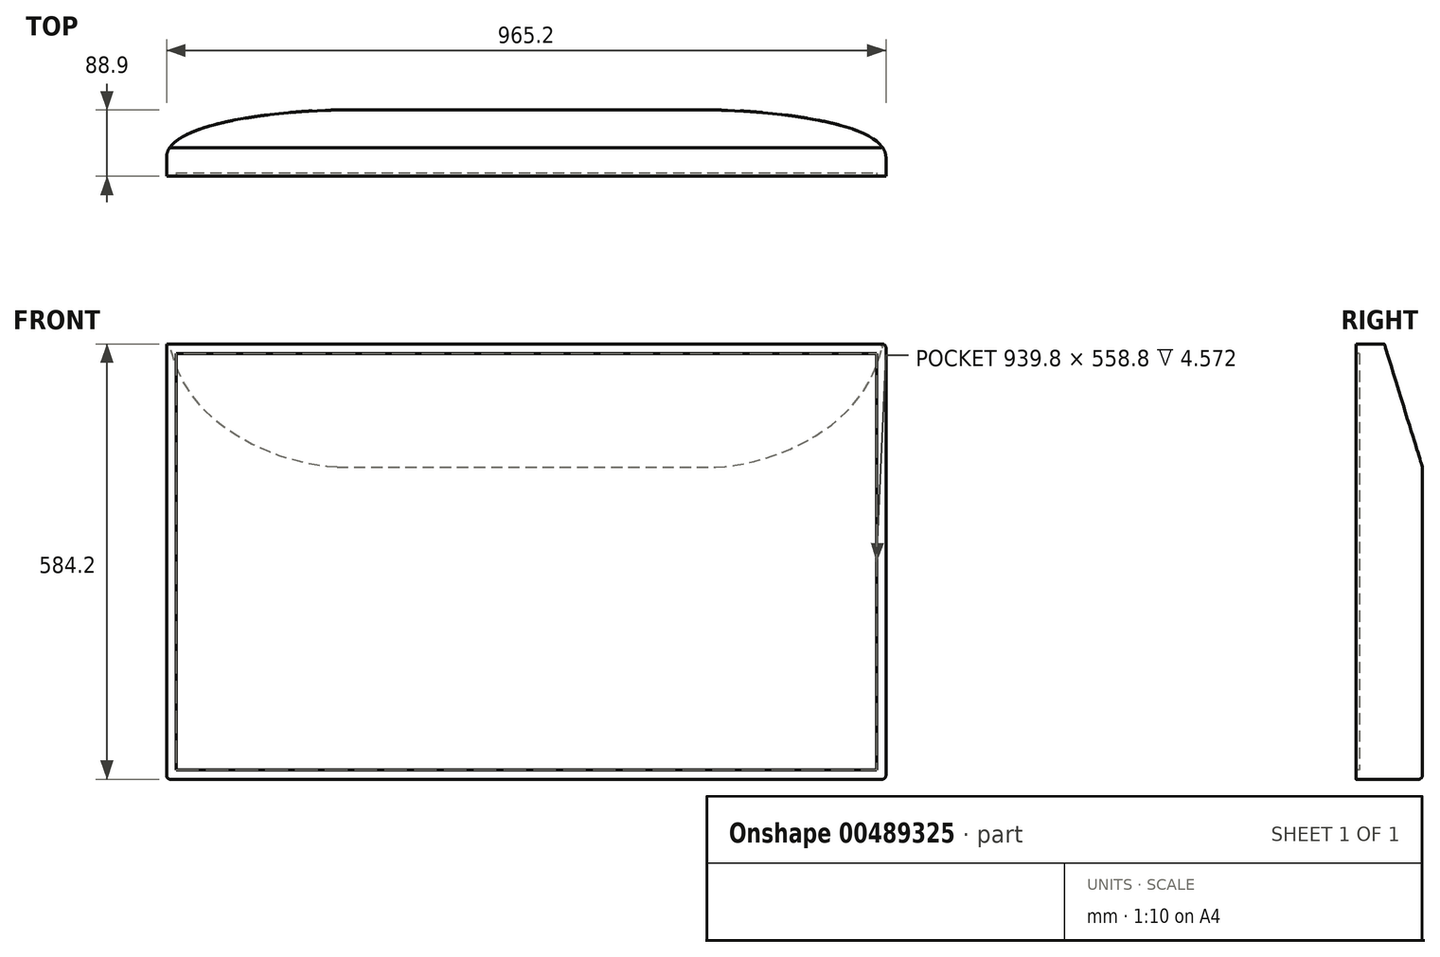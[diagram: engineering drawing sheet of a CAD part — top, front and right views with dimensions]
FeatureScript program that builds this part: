
annotation { "Feature Type Name" : "Feature", "Feature Type Description" : "" }
export const myFeature = defineFeature(function(context is Context, id is Id, definition is map)
    precondition{}
    {
        {
            var Q0;
            Q0=qCreatedBy(makeId("Top.planeOp"),FACE);
            var sketch = newSketch(context, id + "F0", { "sketchPlane" : qUnion([Q0])});
            skLineSegment(sketch, "E0", {"start": v(-482.6, 0) * mm, "end": v(482.6, 0) * mm});
            skLineSegment(sketch, "E1", {"start": v(482.6, 0) * mm, "end": v(482.6, 25.4) * mm});
            skLineSegment(sketch, "E2", {"start": v(-482.6, 0) * mm, "end": v(-482.6, 25.4) * mm});
            skLineSegment(sketch, "E3", {"start": v(-254, 88.9) * mm, "end": v(254, 88.9) * mm});
            skFitSpline(sketch, "E4", {"points": [v(-482.6, 25.4) * mm, v(-254, 88.9) * mm], "startDerivative": vector(0, 152.4) * mm, "endDerivative": vector(152.4, 0) * mm});
            skFitSpline(sketch, "E5.MirrorCS", {"points": [v(482.6, 25.4) * mm, v(254, 88.9) * mm], "startDerivative": vector(0, 152.4) * mm, "endDerivative": vector(-152.4, 0) * mm});
            skSolve(sketch);
        }
        {
            var Q0;
            Q0=makeQuery(id+"F0.imprint","IMPRINT",FACE,{"disambiguationData":[TD([[makeQuery(id+"F0.imprint","IMPRINT",EDGE,{"derivedFrom":sQuery(id+"F0.wireOp",EDGE,"E0")}),1.0]])]});
            extrude(context, id + "F1", {"entities" : qUnion([Q0]), "endBound" : BoundingType.SYMMETRIC, "depth" : 584.2 * mm});
        }
        {
            var Q0;
            Q0=qCreatedBy(makeId("Right.planeOp"),FACE);
            var sketch = newSketch(context, id + "F2", { "sketchPlane" : qUnion([Q0])});
            skLineSegment(sketch, "E6", {"start": v(38.1, 292.1) * mm, "end": v(88.9, 127) * mm});
            skLineSegment(sketch, "E7", {"start": v(88.9, 127) * mm, "end": v(88.9, 292.1) * mm});
            skLineSegment(sketch, "E8", {"start": v(88.9, 292.1) * mm, "end": v(38.1, 292.1) * mm});
            skSolve(sketch);
        }
        {
            var Q0;
            Q0=makeQuery(id+"F2.imprint","IMPRINT",FACE,{"disambiguationData":[TD([[makeQuery(id+"F2.imprint","IMPRINT",EDGE,{"derivedFrom":sQuery(id+"F2.wireOp",EDGE,"E6")}),1.0]])]});
            extrude(context, id + "F3", {"entities" : qUnion([Q0]), "operationType" : NewBodyOperationType.REMOVE, "endBound" : BoundingType.THROUGH_ALL, "oppositeDirection" : true, "depth" : 25.4 * mm, "hasSecondDirection" : true, "secondDirectionBound" : SecondDirectionBoundingType.THROUGH_ALL, "secondDirectionOppositeDirection" : false, "secondDirectionDepth" : 25.4 * mm});
        }
        {
            var Q0;
            Q0=qCreatedBy(makeId("Front.planeOp"),FACE);
            var sketch = newSketch(context, id + "F4", { "sketchPlane" : qUnion([Q0])});
            skLineSegment(sketch, "E9.0", {"start": v(-469.9, -279.4) * mm, "end": v(469.9, -279.4) * mm});
            skLineSegment(sketch, "E9.1", {"start": v(-469.9, 279.4) * mm, "end": v(-469.9, -279.4) * mm});
            skLineSegment(sketch, "E9.2", {"start": v(469.9, 279.4) * mm, "end": v(-469.9, 279.4) * mm});
            skLineSegment(sketch, "E9.3", {"start": v(469.9, -279.4) * mm, "end": v(469.9, 279.4) * mm});
            skSolve(sketch);
        }
        {
            var Q0;
            Q0=makeQuery(id+"F4.imprint","IMPRINT",FACE,{"disambiguationData":[TD([[makeQuery(id+"F4.imprint","IMPRINT",EDGE,{"derivedFrom":sQuery(id+"F4.wireOp",EDGE,"E9.0")}),1.0]])]});
            extrude(context, id + "F5", {"entities" : qUnion([Q0]), "operationType" : NewBodyOperationType.REMOVE, "oppositeDirection" : true, "depth" : 4.57 * mm});
        }
        {
            var Q0;
            Q0=makeQuery(id+"F1.opExtrude","CAP_EDGE",EDGE,{"disambiguationData":[OSD([sQuery(id+"F0.wireOp",EDGE,"E5.MirrorCS")])],"isStart":true});
            var Q1;
            Q1=makeQuery(id+"F1.opExtrude","CAP_EDGE",EDGE,{"disambiguationData":[OSD([sQuery(id+"F0.wireOp",EDGE,"E1")])],"isStart":false});
            var Q2;
            Q2=makeQuery(id+"F3.boolean.opBoolean","COPY",EDGE,{"derivedFrom":makeQuery(id+"F3.opExtrude","SWEPT_EDGE",EDGE,{"disambiguationData":[OSD([sQuery(id+"F2.wireOp",EDGE,"E6"),sQuery(id+"F2.wireOp",EDGE,"E8")])]})});
            fillet(context, id + "F6", {"entities" : qUnion([Q0, Q1, Q2]), "radius" : 5.08 * mm, "tangentPropagation" : true, "allowEdgeOverflow" : false});
        }
    });
